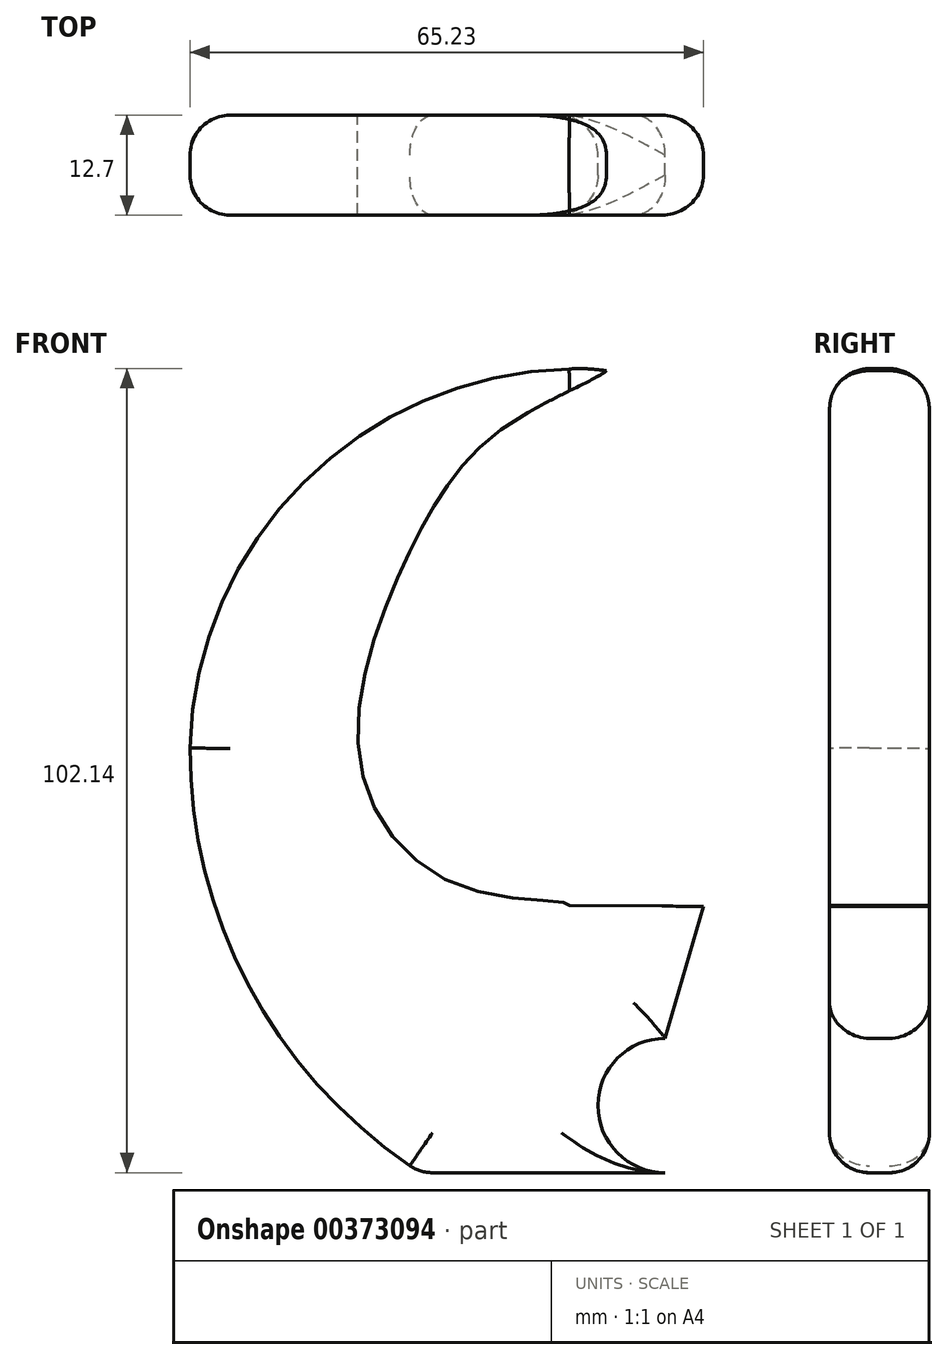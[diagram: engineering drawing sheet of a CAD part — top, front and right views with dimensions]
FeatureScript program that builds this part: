
annotation { "Feature Type Name" : "Feature", "Feature Type Description" : "" }
export const myFeature = defineFeature(function(context is Context, id is Id, definition is map)
    precondition{}
    {
        {
            var Q0;
            Q0=qCreatedBy(makeId("Front.planeOp"),FACE);
            var sketch = newSketch(context, id + "F0", { "sketchPlane" : qUnion([Q0])});
            skLineSegment(sketch, "E0", {"start": v(-18.9, -44.65) * mm, "end": v(12.2, -44.65) * mm});
            skArc(sketch, "E1", {"start": v(-48.16, 9.3) * mm, "mid": v(-40.41, -21.41) * mm, "end": v(-18.9, -44.65) * mm});
            skArc(sketch, "E2", {"start": v(0, 57.45) * mm, "mid": v(-33.73, 43.02) * mm, "end": v(-48.16, 9.3) * mm});
            skFitSpline(sketch, "E3", {"points": [v(0, 57.45) * mm, v(4.88, 57.45) * mm, v(-6.7, 51.05) * mm, v(-16.15, 41.6) * mm, v(-22.56, 29.1) * mm, v(-26.52, 7.16) * mm, v(-13.41, -8.38) * mm, v(0, -10.52) * mm, v(0, -10.82) * mm], "startDerivative": vector(89.22, 8.63) * mm, "endDerivative": vector(-6.99, -15.86) * mm});
            skArc(sketch, "E4", {"start": v(12.2, -27.58) * mm, "mid": v(3.66, -36.12) * mm, "end": v(12.2, -44.65) * mm});
            skLineSegment(sketch, "E5", {"start": v(12.2, -27.58) * mm, "end": v(17.07, -10.82) * mm});
            skLineSegment(sketch, "E6", {"start": v(0.05, -10.71) * mm, "end": v(0.04, -10.71) * mm});
            skLineSegment(sketch, "E7", {"start": v(0.05, -10.71) * mm, "end": v(17.07, -10.82) * mm});
            skFitSpline(sketch, "E8", {"points": [v(0, 57.45) * mm, v(2.46, 57.45) * mm, v(5.79, 57.06) * mm, v(5.96, 57) * mm], "startDerivative": vector(5.16, 0.25) * mm, "endDerivative": vector(0.92, -0.46) * mm});
            skSolve(sketch);
        }
        {
            var Q0;
            Q0=makeQuery(id+"F0.imprint","IMPRINT",FACE,{"disambiguationData":[TD([[makeQuery(id+"F0.imprint","IMPRINT",EDGE,{"derivedFrom":sQuery(id+"F0.wireOp",EDGE,"E0")}),1.0]])]});
            extrude(context, id + "F1", {"entities" : qUnion([Q0]), "depth" : 12.7 * mm});
        }
        {
            var Q0;
            Q0=makeQuery(id+"F1.opExtrude","CAP_EDGE",EDGE,{"disambiguationData":[OSD([sQuery(id+"F0.wireOp",EDGE,"E2")])],"isStart":true});
            var Q1;
            Q1=makeQuery(id+"F1.opExtrude","CAP_EDGE",EDGE,{"disambiguationData":[OSD([sQuery(id+"F0.wireOp",EDGE,"E1")])],"isStart":true});
            var Q2;
            Q2=makeQuery(id+"F1.opExtrude","CAP_EDGE",EDGE,{"disambiguationData":[OSD([sQuery(id+"F0.wireOp",EDGE,"E2")])],"isStart":false});
            var Q3;
            Q3=makeQuery(id+"F1.opExtrude","CAP_EDGE",EDGE,{"disambiguationData":[OSD([sQuery(id+"F0.wireOp",EDGE,"E1")])],"isStart":false});
            fillet(context, id + "F2", {"entities" : qUnion([Q0, Q1, Q2, Q3]), "radius" : 5.08 * mm, "tangentPropagation" : true, "allowEdgeOverflow" : false});
        }
        {
            var Q0;
            Q0=makeQuery(id+"F1.opExtrude","CAP_EDGE",EDGE,{"disambiguationData":[OSD([sQuery(id+"F0.wireOp",EDGE,"E5")])],"isStart":false});
            var Q1;
            Q1=makeQuery(id+"F1.opExtrude","CAP_EDGE",EDGE,{"disambiguationData":[OSD([sQuery(id+"F0.wireOp",EDGE,"E5")])],"isStart":true});
            var Q2;
            Q2=makeQuery(id+"F1.opExtrude","CAP_EDGE",EDGE,{"disambiguationData":[OSD([sQuery(id+"F0.wireOp",EDGE,"E4")])],"isStart":true});
            var Q3;
            Q3=makeQuery(id+"F1.opExtrude","CAP_EDGE",EDGE,{"disambiguationData":[OSD([sQuery(id+"F0.wireOp",EDGE,"E4")])],"isStart":false});
            var Q4;
            Q4=makeQuery(id+"F1.opExtrude","CAP_EDGE",EDGE,{"disambiguationData":[OSD([sQuery(id+"F0.wireOp",EDGE,"E0")])],"isStart":false});
            fillet(context, id + "F3", {"entities" : qUnion([Q0, Q1, Q2, Q3, Q4]), "radius" : 5.08 * mm, "tangentPropagation" : true, "allowEdgeOverflow" : false});
        }
    });
